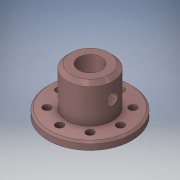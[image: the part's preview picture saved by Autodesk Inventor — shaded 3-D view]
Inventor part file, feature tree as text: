
AUTODESK INVENTOR PART (.ipt)
format: ipt  version: 2016 (Build 200138000, 138)  size: 174,080 bytes
history: native  units: mm
features: other x3, extrude x1, sketch x1
ambient origin geometry x8: Origin, YZ Plane, XZ Plane, XY Plane, X Axis, Y Axis, Z Axis, Center Point
bodies: Solid1 (feature_tree)
feature tree (5):
  other  "Servo-Dynamixel-Adapter.ipt"
  extrude  "Extrusion1"  Depth=3.0mm
  other  "Solid1::Servo-Dynamixel-Adapter.ipt"
  other  "TaggingFeature1"
  sketch  "Sketch1"  dims[d0=10.0mm d1=8.5mm d2=3.0mm d3=0.0mm]
